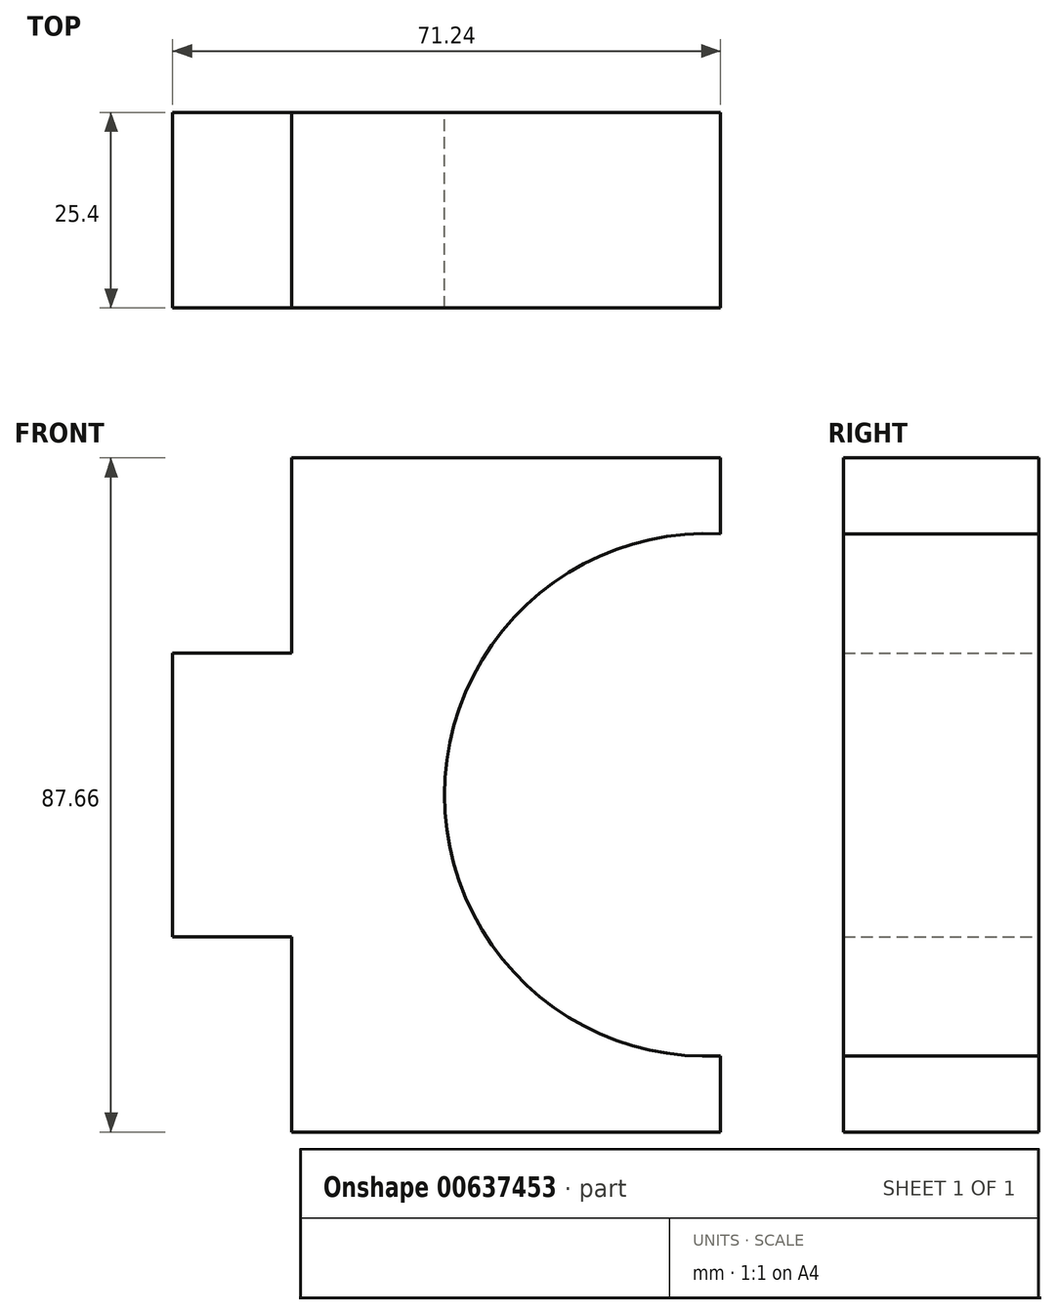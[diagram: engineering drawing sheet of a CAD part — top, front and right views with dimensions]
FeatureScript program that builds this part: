
annotation { "Feature Type Name" : "Feature", "Feature Type Description" : "" }
export const myFeature = defineFeature(function(context is Context, id is Id, definition is map)
    precondition{}
    {
        {
            var Q0;
            Q0=qCreatedBy(makeId("Front.planeOp"),FACE);
            var sketch = newSketch(context, id + "F0", { "sketchPlane" : qUnion([Q0])});
            skLineSegment(sketch, "E0", {"start": v(-7.98, 54.85) * mm, "end": v(-63.74, 54.85) * mm});
            skLineSegment(sketch, "E1", {"start": v(-63.74, 54.85) * mm, "end": v(-63.74, 29.45) * mm});
            skLineSegment(sketch, "E2", {"start": v(-63.74, 29.45) * mm, "end": v(-79.22, 29.45) * mm});
            skLineSegment(sketch, "E3", {"start": v(-79.22, 29.45) * mm, "end": v(-79.22, -7.41) * mm});
            skLineSegment(sketch, "E4", {"start": v(-79.22, -7.41) * mm, "end": v(-63.74, -7.41) * mm});
            skLineSegment(sketch, "E5", {"start": v(-63.74, -7.41) * mm, "end": v(-63.74, -32.81) * mm});
            skLineSegment(sketch, "E6", {"start": v(-63.74, -32.81) * mm, "end": v(-7.98, -32.81) * mm});
            skLineSegment(sketch, "E7", {"start": v(-7.98, -32.81) * mm, "end": v(-7.98, -22.9) * mm});
            skLineSegment(sketch, "E8", {"start": v(-7.98, 54.85) * mm, "end": v(-7.98, 44.94) * mm});
            skArc(sketch, "E9", {"start": v(-7.98, 44.94) * mm, "mid": v(-43.88, 11.02) * mm, "end": v(-7.98, -22.9) * mm});
            skSolve(sketch);
        }
        {
            var Q0;
            Q0 = qSketchRegion(id + "F0", true);
            extrude(context, id + "F1", {"entities" : qUnion([Q0]), "depth" : 25.4 * mm, "offsetDistance" : 25.4 * mm});
        }
    });
